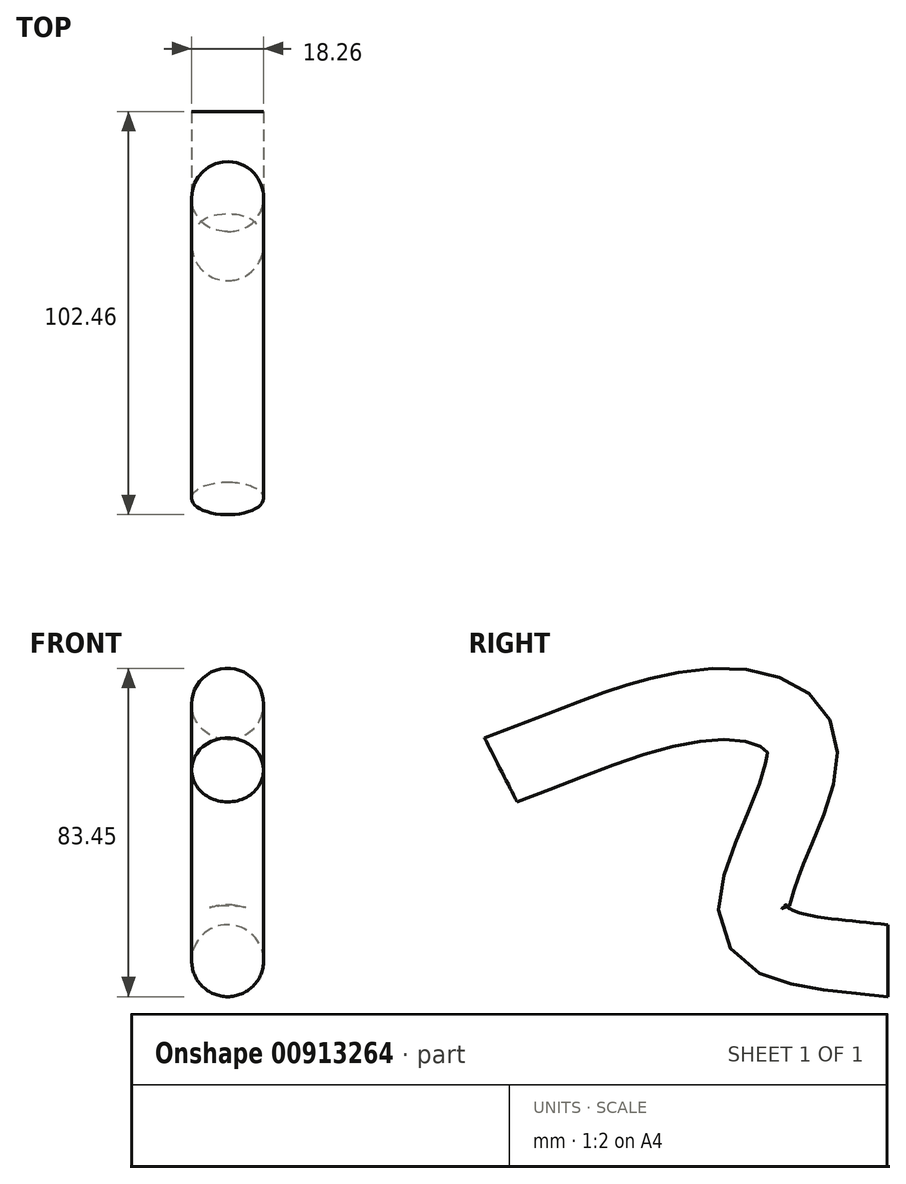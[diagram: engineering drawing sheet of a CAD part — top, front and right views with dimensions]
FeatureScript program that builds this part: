
annotation { "Feature Type Name" : "Feature", "Feature Type Description" : "" }
export const myFeature = defineFeature(function(context is Context, id is Id, definition is map)
    precondition{}
    {
        {
            var Q0;
            Q0=qCreatedBy(makeId("Front.planeOp"),FACE);
            var sketch = newSketch(context, id + "F0", { "sketchPlane" : qUnion([Q0])});
            skCircle(sketch, "E0", {"center": v(0, 0) * mm, "radius": 9.13 * mm});
            skSolve(sketch);
        }
        {
            var Q0;
            Q0=qCreatedBy(makeId("Right.planeOp"),FACE);
            var sketch = newSketch(context, id + "F1", { "sketchPlane" : qUnion([Q0])});
            skFitSpline(sketch, "E1", {"points": [v(0, 0) * mm, v(-33.61, 10.62) * mm, v(-21.9, 53.5) * mm, v(-43.33, 65.22) * mm, v(-98.31, 48.5) * mm], "startDerivative": vector(-188.83, 23.39) * mm, "endDerivative": vector(-185.95, -67.41) * mm});
            skSolve(sketch);
        }
        {
            var Q0;
            Q0=makeQuery(id+"F0.imprint","IMPRINT",FACE,{"disambiguationData":[TD([[makeQuery(id+"F0.imprint","IMPRINT",EDGE,{"derivedFrom":sQuery(id+"F0.wireOp",EDGE,"E0")}),1.0]])]});
            var Q1;
            Q1=sQuery(id+"F1.wireOp",EDGE,"E1");
            sweep(context, id + "F2", {"profiles" : qUnion([Q0]), "path" : qUnion([Q1])});
        }
    });
